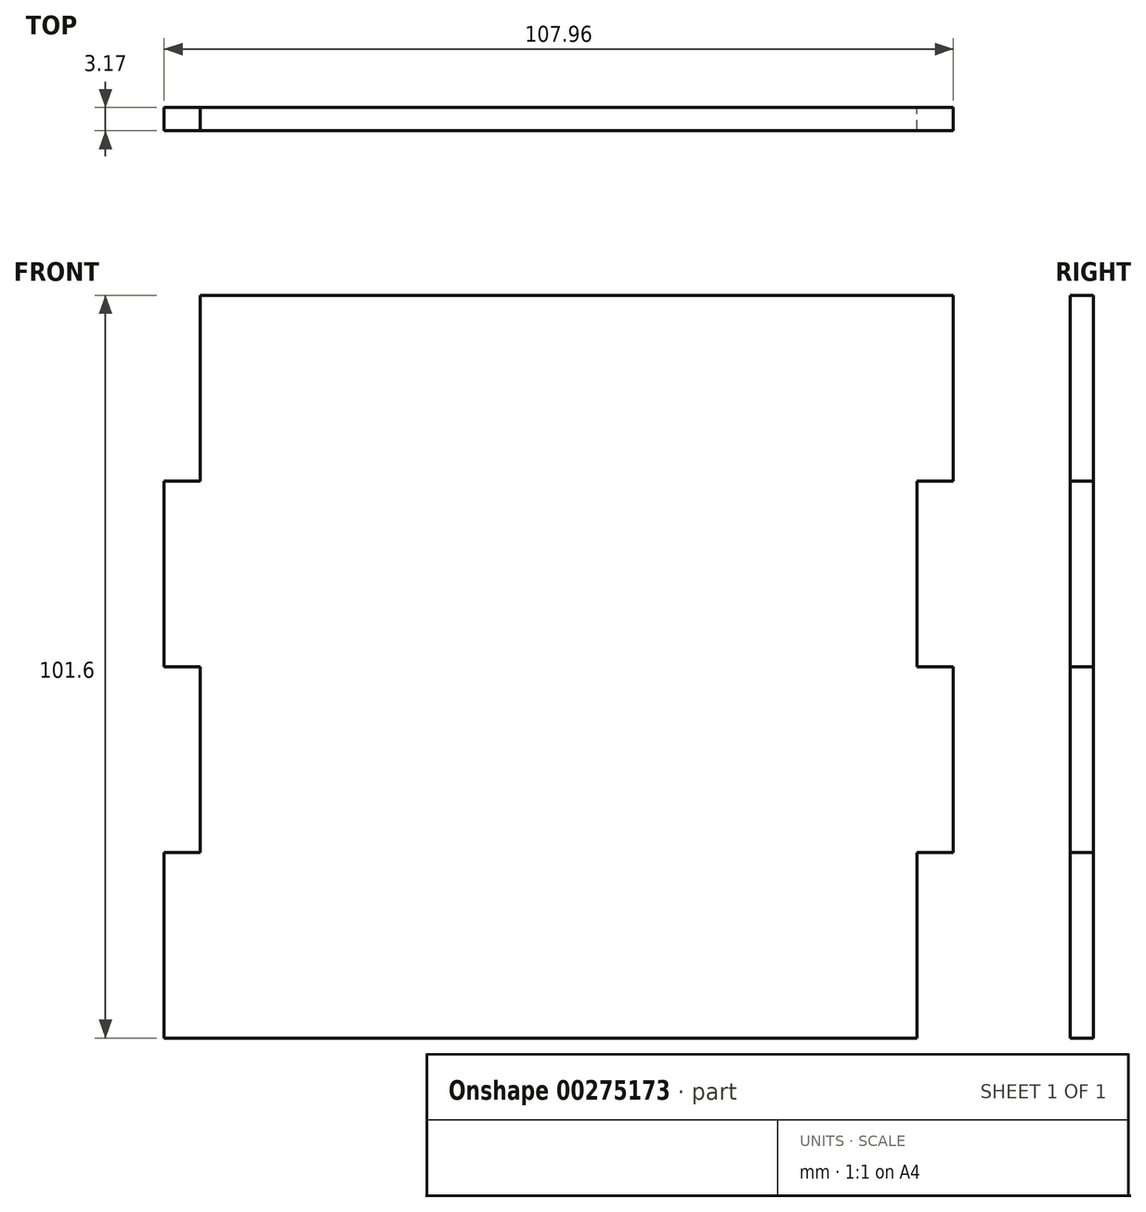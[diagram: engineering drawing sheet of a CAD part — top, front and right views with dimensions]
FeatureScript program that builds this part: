
annotation { "Feature Type Name" : "Feature", "Feature Type Description" : "" }
export const myFeature = defineFeature(function(context is Context, id is Id, definition is map)
    precondition{}
    {
        {
            var Q0;
            Q0=qCreatedBy(makeId("Front.planeOp"),FACE);
            var sketch = newSketch(context, id + "F0", { "sketchPlane" : qUnion([Q0])});
            skLineSegment(sketch, "E0.bottom", {"start": v(50.8, -39.82) * mm, "end": v(-50.8, -39.82) * mm});
            skLineSegment(sketch, "E0.top", {"start": v(50.8, 61.78) * mm, "end": v(-50.8, 61.78) * mm});
            skLineSegment(sketch, "E0.left", {"start": v(50.8, -39.82) * mm, "end": v(50.8, 61.78) * mm});
            skLineSegment(sketch, "E0.right", {"start": v(-50.8, -39.82) * mm, "end": v(-50.8, 61.78) * mm});
            skLineSegment(sketch, "E1.bottom", {"start": v(50.8, -39.82) * mm, "end": v(25.4, -39.82) * mm});
            skLineSegment(sketch, "E1.top", {"start": v(50.8, -43) * mm, "end": v(25.4, -43) * mm});
            skLineSegment(sketch, "E1.left", {"start": v(50.8, -39.82) * mm, "end": v(50.8, -43) * mm});
            skLineSegment(sketch, "E1.right", {"start": v(25.4, -39.82) * mm, "end": v(25.4, -43) * mm});
            skLineSegment(sketch, "E2.bottom", {"start": v(0, -39.82) * mm, "end": v(-25.4, -39.82) * mm});
            skLineSegment(sketch, "E2.top", {"start": v(0, -43) * mm, "end": v(-25.4, -43) * mm});
            skLineSegment(sketch, "E2.left", {"start": v(0, -39.82) * mm, "end": v(0, -43) * mm});
            skLineSegment(sketch, "E2.right", {"start": v(-25.4, -39.82) * mm, "end": v(-25.4, -43) * mm});
            skSolve(sketch);
        }
        {
            var Q0;
            Q0=makeQuery(id+"F0.imprint","IMPRINT",FACE,{"disambiguationData":[TD([[makeQuery(id+"F0.imprint","IMPRINT",EDGE,{"derivedFrom":sQuery(id+"F0.wireOp",EDGE,"E0.top")}),1.0]])]});
            var Q1;
            Q1=makeQuery(id+"F0.imprint","IMPRINT",FACE,{"disambiguationData":[TD([[makeQuery(id+"F0.imprint","IMPRINT",EDGE,{"derivedFrom":sQuery(id+"F0.wireOp",EDGE,"E2.bottom")}),1.0]])]});
            var Q2;
            Q2=makeQuery(id+"F0.imprint","IMPRINT",FACE,{"disambiguationData":[TD([[makeQuery(id+"F0.imprint","IMPRINT",EDGE,{"derivedFrom":sQuery(id+"F0.wireOp",EDGE,"E1.bottom")}),1.0]])]});
            extrude(context, id + "F1", {"entities" : qUnion([Q0, Q1, Q2]), "depth" : 3.17 * mm});
        }
        {
            var Q0;
            Q0=makeQuery(id+"F1.opExtrude","CAP_FACE",FACE,{"disambiguationData":[OSD([sQuery(id+"F0.wireOp",EDGE,"E0.bottom"),sQuery(id+"F0.wireOp",EDGE,"E0.top"),sQuery(id+"F0.wireOp",EDGE,"E0.left"),sQuery(id+"F0.wireOp",EDGE,"E0.right"),sQuery(id+"F0.wireOp",EDGE,"E1.top"),sQuery(id+"F0.wireOp",EDGE,"E1.left"),sQuery(id+"F0.wireOp",EDGE,"E1.right"),sQuery(id+"F0.wireOp",EDGE,"E2.top"),sQuery(id+"F0.wireOp",EDGE,"E2.left"),sQuery(id+"F0.wireOp",EDGE,"E2.right")])],"isStart":false});
            var sketch = newSketch(context, id + "F2", { "sketchPlane" : qUnion([Q0])});
            skLineSegment(sketch, "E3", {"start": v(-92.75, 36.38) * mm, "end": v(114.4, 36.38) * mm, "construction": true});
            skLineSegment(sketch, "E4", {"start": v(-92.4, 10.98) * mm, "end": v(116.87, 10.98) * mm, "construction": true});
            skLineSegment(sketch, "E5", {"start": v(-90.98, -14.42) * mm, "end": v(119.71, -14.42) * mm, "construction": true});
            skLineSegment(sketch, "E6", {"start": v(-93.46, 61.78) * mm, "end": v(114.04, 61.78) * mm, "construction": true});
            skLineSegment(sketch, "E7", {"start": v(-91.5, -39.82) * mm, "end": v(97.43, -39.82) * mm, "construction": true});
            skLineSegment(sketch, "E8.0", {"start": v(53.97, -43) * mm, "end": v(53.97, 61.78) * mm});
            skLineSegment(sketch, "E9.0", {"start": v(-53.98, -39.82) * mm, "end": v(-53.98, 61.78) * mm});
            skLineSegment(sketch, "E10", {"start": v(53.97, 61.78) * mm, "end": v(50.8, 61.78) * mm});
            skLineSegment(sketch, "E11", {"start": v(53.97, 36.38) * mm, "end": v(50.8, 36.38) * mm});
            skLineSegment(sketch, "E12", {"start": v(53.97, 10.98) * mm, "end": v(50.8, 10.98) * mm});
            skLineSegment(sketch, "E13", {"start": v(53.97, -14.42) * mm, "end": v(50.8, -14.42) * mm});
            skLineSegment(sketch, "E14", {"start": v(-50.8, -39.82) * mm, "end": v(-53.98, -39.82) * mm});
            skLineSegment(sketch, "E15", {"start": v(-50.8, -14.42) * mm, "end": v(-53.98, -14.42) * mm});
            skLineSegment(sketch, "E16", {"start": v(-50.8, 10.98) * mm, "end": v(-53.98, 10.98) * mm});
            skLineSegment(sketch, "E17", {"start": v(-53.98, 36.38) * mm, "end": v(-50.8, 36.38) * mm});
            skSolve(sketch);
        }
        {
            var Q0;
            {var subQ0=sQuery(id+"F2.wireOp",EDGE,"E16");Q0=makeQuery(id+"F2.imprint","IMPRINT",FACE,{"disambiguationData":[TD([[makeQuery(id+"F2.imprint","IMPRINT",EDGE,{"derivedFrom":subQ0}),-1.0]])]});}
            var Q1;
            {var subQ0=sQuery(id+"F2.wireOp",EDGE,"E14");Q1=makeQuery(id+"F2.imprint","IMPRINT",FACE,{"disambiguationData":[TD([[makeQuery(id+"F2.imprint","IMPRINT",EDGE,{"derivedFrom":subQ0}),-1.0]])]});}
            var Q2;
            {var subQ0=sQuery(id+"F2.wireOp",EDGE,"E10");Q2=makeQuery(id+"F2.imprint","IMPRINT",FACE,{"disambiguationData":[TD([[makeQuery(id+"F2.imprint","IMPRINT",EDGE,{"derivedFrom":subQ0}),1.0]])]});}
            var Q3;
            {var subQ0=sQuery(id+"F2.wireOp",EDGE,"E12");Q3=makeQuery(id+"F2.imprint","IMPRINT",FACE,{"disambiguationData":[TD([[makeQuery(id+"F2.imprint","IMPRINT",EDGE,{"derivedFrom":subQ0}),1.0]])]});}
            extrude(context, id + "F3", {"entities" : qUnion([Q0, Q1, Q2, Q3]), "operationType" : NewBodyOperationType.ADD, "oppositeDirection" : true, "depth" : 3.17 * mm});
        }
        {
            var Q0;
            {var subQ0=sQuery(id+"F2.wireOp",EDGE,"E9.0");var subQ1=sQuery(id+"F0.wireOp",EDGE,"E0.right");var subQ2=sQuery(id+"F2.wireOp",EDGE,"E8.0");var subQ3=sQuery(id+"F0.wireOp",EDGE,"E1.left");var subQ4=sQuery(id+"F0.wireOp",EDGE,"E0.left");Q0=makeQuery(id+"F3.boolean.opBoolean","MERGE",FACE,{"derivedFrom":[makeQuery(id+"F1.opExtrude","CAP_FACE",FACE,{"disambiguationData":[OSD([sQuery(id+"F0.wireOp",EDGE,"E0.bottom"),sQuery(id+"F0.wireOp",EDGE,"E0.top"),subQ4,subQ1,sQuery(id+"F0.wireOp",EDGE,"E1.top"),subQ3,sQuery(id+"F0.wireOp",EDGE,"E1.right"),sQuery(id+"F0.wireOp",EDGE,"E2.top"),sQuery(id+"F0.wireOp",EDGE,"E2.left"),sQuery(id+"F0.wireOp",EDGE,"E2.right")])],"isStart":true}),makeQuery(id+"F3.opExtrude","CAP_FACE",FACE,{"disambiguationData":[OSD([subQ4,subQ3,subQ2,sQuery(id+"F2.wireOp",EDGE,"E12"),sQuery(id+"F2.wireOp",EDGE,"E13")])],"isStart":false}),makeQuery(id+"F3.opExtrude","CAP_FACE",FACE,{"disambiguationData":[OSD([subQ4,subQ3,subQ2,sQuery(id+"F2.wireOp",EDGE,"E10"),sQuery(id+"F2.wireOp",EDGE,"E11")])],"isStart":false}),makeQuery(id+"F3.opExtrude","CAP_FACE",FACE,{"disambiguationData":[OSD([subQ1,subQ0,sQuery(id+"F2.wireOp",EDGE,"E14"),sQuery(id+"F2.wireOp",EDGE,"E15")])],"isStart":false}),makeQuery(id+"F3.opExtrude","CAP_FACE",FACE,{"disambiguationData":[OSD([subQ1,subQ0,sQuery(id+"F2.wireOp",EDGE,"E16"),sQuery(id+"F2.wireOp",EDGE,"E17")])],"isStart":false})]});}
            var sketch = newSketch(context, id + "F4", { "sketchPlane" : qUnion([Q0])});
            skLineSegment(sketch, "E18.0", {"start": v(-49.02, 10.98) * mm, "end": v(-49.02, 36.38) * mm});
            skLineSegment(sketch, "E19.0", {"start": v(-49.02, -43) * mm, "end": v(-49.02, -14.42) * mm});
            skLineSegment(sketch, "E20.0", {"start": v(49.02, 36.38) * mm, "end": v(49.02, 61.78) * mm});
            skLineSegment(sketch, "E21.0", {"start": v(49.02, -14.42) * mm, "end": v(49.02, 10.98) * mm});
            skLineSegment(sketch, "E22", {"start": v(-49.02, 36.38) * mm, "end": v(-50.8, 36.38) * mm});
            skLineSegment(sketch, "E23", {"start": v(-50.8, 36.38) * mm, "end": v(-50.8, 10.98) * mm});
            skLineSegment(sketch, "E24", {"start": v(-50.8, 10.98) * mm, "end": v(-49.02, 10.98) * mm});
            skLineSegment(sketch, "E25", {"start": v(-49.02, -14.42) * mm, "end": v(-50.8, -14.42) * mm});
            skLineSegment(sketch, "E26", {"start": v(-50.8, -14.42) * mm, "end": v(-50.8, -43) * mm});
            skLineSegment(sketch, "E27", {"start": v(-50.8, -43) * mm, "end": v(-49.02, -43) * mm});
            skLineSegment(sketch, "E28", {"start": v(49.02, 10.98) * mm, "end": v(50.8, 10.98) * mm});
            skLineSegment(sketch, "E29", {"start": v(50.8, 10.98) * mm, "end": v(50.8, -14.42) * mm});
            skLineSegment(sketch, "E30", {"start": v(50.8, -14.42) * mm, "end": v(49.02, -14.42) * mm});
            skLineSegment(sketch, "E31", {"start": v(49.02, 61.78) * mm, "end": v(50.8, 61.78) * mm});
            skLineSegment(sketch, "E32", {"start": v(50.8, 61.78) * mm, "end": v(50.8, 36.38) * mm});
            skLineSegment(sketch, "E33", {"start": v(50.8, 36.38) * mm, "end": v(49.02, 36.38) * mm});
            skSolve(sketch);
        }
        {
            var Q0;
            Q0=makeQuery(id+"F4.imprint","IMPRINT",FACE,{"disambiguationData":[TD([[makeQuery(id+"F4.imprint","IMPRINT",EDGE,{"derivedFrom":sQuery(id+"F4.wireOp",EDGE,"E18.0")}),1.0]])]});
            var Q1;
            Q1=makeQuery(id+"F4.imprint","IMPRINT",FACE,{"disambiguationData":[TD([[makeQuery(id+"F4.imprint","IMPRINT",EDGE,{"derivedFrom":sQuery(id+"F4.wireOp",EDGE,"E20.0")}),-1.0]])]});
            var Q2;
            Q2=makeQuery(id+"F4.imprint","IMPRINT",FACE,{"disambiguationData":[TD([[makeQuery(id+"F4.imprint","IMPRINT",EDGE,{"derivedFrom":sQuery(id+"F4.wireOp",EDGE,"E21.0")}),-1.0]])]});
            var Q3;
            Q3=makeQuery(id+"F4.imprint","IMPRINT",FACE,{"disambiguationData":[TD([[makeQuery(id+"F4.imprint","IMPRINT",EDGE,{"derivedFrom":sQuery(id+"F4.wireOp",EDGE,"E19.0")}),1.0]])]});
            extrude(context, id + "F5", {"entities" : qUnion([Q0, Q1, Q2, Q3]), "operationType" : NewBodyOperationType.REMOVE, "oppositeDirection" : true, "depth" : 3.17 * mm});
        }
    });
